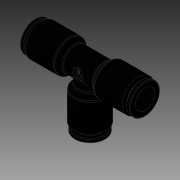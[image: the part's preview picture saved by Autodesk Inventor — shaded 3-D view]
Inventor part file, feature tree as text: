
AUTODESK INVENTOR PART (.ipt)
format: ipt  version: 2016 SP1 (Build 200210100, 210)  size: 258,560 bytes
history: native  units: in
note: dims shown in document units (in); Inventor stores cm internally (conversion verified against a paired STEP export)
features: extrude x2, sketch x2
ambient origin geometry x8: Origin, YZ Plane, XZ Plane, XY Plane, X Axis, Y Axis, Z Axis, Center Point
bodies: Solid1 (feature_tree)
feature tree (4):
  extrude  "Extrusion1"  Depth=1.0in TaperAngle=0.0deg
  extrude  "Extrusion2"  Depth=0.578in TaperAngle=0.0deg
  sketch  "Sketch1"  dims[d0=0.25in d1=1.0in d2=0.0in]
  sketch  "Sketch2"  dims[d3=0.25in d4=0.578in d5=0.0in]
